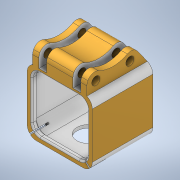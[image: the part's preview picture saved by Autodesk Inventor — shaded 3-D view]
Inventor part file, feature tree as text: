
AUTODESK INVENTOR PART (.ipt)
format: ipt  version: 2020 (Build 240168000, 168)  size: 339,456 bytes
history: native  units: in
note: dims shown in document units (in); Inventor stores cm internally (conversion verified against a paired STEP export)
features: extrude x5, sketch x5, other x3, projected_geometry x3, fillet x2
ambient origin geometry x8: Origin, YZ Plane, XZ Plane, XY Plane, X Axis, Y Axis, Z Axis, Center Point
bodies: Solid1 (feature_tree)
feature tree (18):
  other  "Assembly4.iam"
  other  "Kauri modular session 5 mount.ipt:1"
  other  "session 5.ipt:1"
  extrude  "Extrusion1"  Depth=0.3937in TaperAngle=0.0deg
  extrude  "Extrusion2"  Depth=1.0in TaperAngle=0.0deg
  extrude  "Extrusion3"  Depth=0.3937in TaperAngle=0.0deg
  fillet  "Fillet1"  Radius=0.2362in
  fillet  "Fillet2"  Radius=0.0394in
  extrude  "Extrusion4"  Depth=0.3937in
  extrude  "Extrusion5"  Depth=0.1969in
  sketch  "Sketch1"  dims[d0=0.3937in d1=1.0in d2=0.0in]
  projected_geometry  "Projected Loop1"
  sketch  "Sketch2"  dims[d3=0.5906in d4=1.0in d5=0.0in]
  sketch  "Sketch3"  dims[d6=0.9843in d7=0.3937in d8=0.0in d9=0.2362in d10=0.0394in]
  projected_geometry  "Projected Loop2"
  sketch  "Sketch4"  dims[d12=0.0197in d15=0.3937in d16=0.0in d17=0.0197in]
  projected_geometry  "Projected Loop3"
  sketch  "Sketch5"  dims[d18=0.0197in d19=0.0197in d20=0.0197in d21=0.1575in d22=0.1575in d23=0.1575in d24=0.0in d25=0.0in d26=0.1969in d27=0.1969in]
